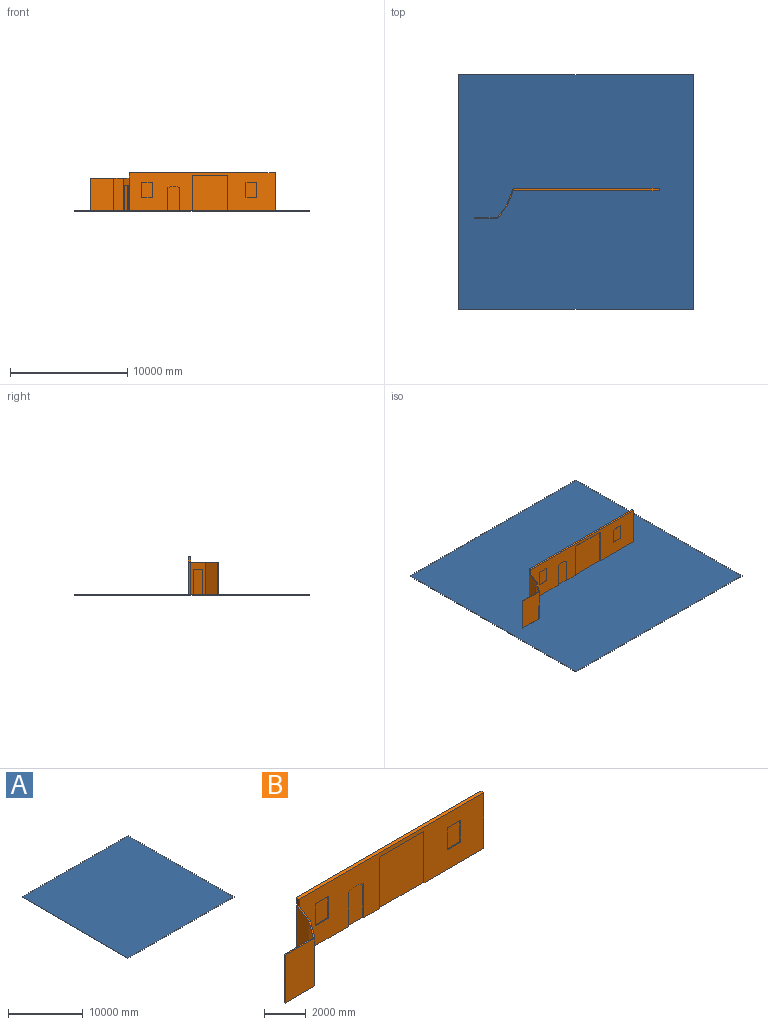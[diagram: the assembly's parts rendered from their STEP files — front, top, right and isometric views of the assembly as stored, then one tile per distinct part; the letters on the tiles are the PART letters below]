
ASSEMBLY  parts=2 mates=1
PART A: 6 faces, bbox 20000x20000x25 mm
  f0: plane 20000x25mm, normal (0,-1,0), area 500000mm2, adj f1,f3,f4,f5
  f1: plane 20000x25mm, normal (1,0,0), area 500000mm2, adj f0,f2,f4,f5
  f2: plane 20000x25mm, normal (0,1,0), area 500000mm2, adj f1,f3,f4,f5
  f3: plane 20000x25mm, normal (-1,0,0), area 500000mm2, adj f0,f2,f4,f5
  f4: plane 20000x20000mm, normal (0,0,1), area 400000000mm2, adj f0,f1,f2,f3
  f5: plane 20000x20000mm, normal (0,0,-1), area 400000000mm2, adj f0,f1,f2,f3
PART B: 36 faces, bbox 15730x2538.9x3250 mm
  f0: plane 12430x3250mm, normal (0,-1,0), area 26986392.5mm2, adj f1,f3,f4,f5,f12,f14,f15,f16
  f1: plane 3250x200mm, normal (1,0,0), area 650000mm2, adj f0,f2,f4,f5
  f2: plane 12430x3250mm, normal (0,1,0), area 40397500mm2, adj f1,f3,f4,f5,f6
  f3: plane 450x200mm, normal (-1,0,0), area 90000mm2, adj f0,f2,f4,f13
  f4: plane 12430x200mm, normal (0,0,1), area 2486000mm2, adj f0,f1,f2,f3
  f5: plane 15730x2538.88mm, normal (0,0,-1), area 2578850.3mm2, adj f0,f1,f2,f6,f7,f8,f9,f10
  f6: plane 2800x1415.06mm, normal (-0.93,0.37,0), area 4258106.5mm2, adj f2,f5,f7,f13
  f7: plane 2800x1058.97mm, normal (-0.8,0.6,0), area 3703794.9mm2, adj f5,f6,f8,f13
  f8: plane 2800x1950.27mm, normal (0,1,0), area 5460751.5mm2, adj f5,f7,f9,f13
  f9: plane 2800x64.85mm, normal (-1,0,0), area 181587.6mm2, adj f5,f8,f10,f13
  f10: plane 2800x2000mm, normal (0,-1,0), area 5600000mm2, adj f5,f9,f11,f13
  f11: plane 2800x1068.75mm, normal (0.8,-0.6,0), area 3738000mm2, adj f5,f10,f12,f13
  f12: plane 2800x1270.13mm, normal (0.93,-0.37,0), area 1883850mm2, adj f0,f5,f11,f13,f32,f33,f34
  f13: plane 3300x2538.88mm, normal (0,0,1), area 338350.3mm2, adj f3,f6,f7,f8,f9,f10,f11,f12
  f14: plane 3000x50mm, normal (0,0,-1), area 150000mm2, adj f0,f15,f16,f17
  f15: plane 3000x50mm, normal (1,0,0), area 150000mm2, adj f0,f5,f14,f17
  f16: plane 3000x50mm, normal (-1,0,0), area 150000mm2, adj f0,f5,f14,f17
  f17: plane 3000x3000mm, normal (0,-1,0), area 9000000mm2, adj f5,f14,f15,f16
  f18: cylinder r=1057.5mm len=1025mm, axis (0,-1,0), area 53503.6mm2, adj f0,f19,f20,f21
  f19: plane 1982.75x50mm, normal (1,0,0), area 99137.6mm2, adj f0,f5,f18,f21
  f20: plane 1982.28x50mm, normal (-1,0,0), area 99113.8mm2, adj f0,f5,f18,f21
  f21: plane 2115x1025mm, normal (0,-1,0), area 2123807.5mm2, adj f5,f18,f19,f20
  f22: plane 890x50mm, normal (0,0,-1), area 44500mm2, adj f0,f23,f25,f26
  f23: plane 1285x50mm, normal (1,0,0), area 64250mm2, adj f0,f22,f24,f26
  f24: plane 890x50mm, normal (0,0,1), area 44500mm2, adj f0,f23,f25,f26
  f25: plane 1285x50mm, normal (-1,0,0), area 64250mm2, adj f0,f22,f24,f26
  f26: plane 1285x890mm, normal (0,-1,0), area 1143650mm2, adj f22,f23,f24,f25
  f27: plane 890x50mm, normal (0,0,-1), area 44500mm2, adj f0,f28,f30,f31
  f28: plane 1285x50mm, normal (1,0,0), area 64250mm2, adj f0,f27,f29,f31
  f29: plane 890x50mm, normal (0,0,1), area 44500mm2, adj f0,f28,f30,f31
  f30: plane 1285x50mm, normal (-1,0,0), area 64250mm2, adj f0,f27,f29,f31
  f31: plane 1285x890mm, normal (0,-1,0), area 1143650mm2, adj f27,f28,f29,f30
  f32: plane 841.8x370.7mm, normal (0,0,-1), area 44250mm2, adj f12,f33,f34,f35
  f33: plane 2190x46.53mm, normal (0.37,0.93,0), area 109500mm2, adj f5,f12,f32,f35
  f34: plane 2190x46.53mm, normal (-0.37,-0.93,0), area 109500mm2, adj f5,f12,f32,f35
  f35: plane 2190x823.49mm, normal (0.93,-0.37,0), area 1938150mm2, adj f5,f32,f33,f34
PLACE A t=(-149.44,2235.6,-932.1)mm
PLACE B t=(-3159.09,2088.12,-907.1)mm
MATE fastened A.f4 <-> B.f5  axis (0,0,1) through (-149.44,2235.6,-907.1)mm
